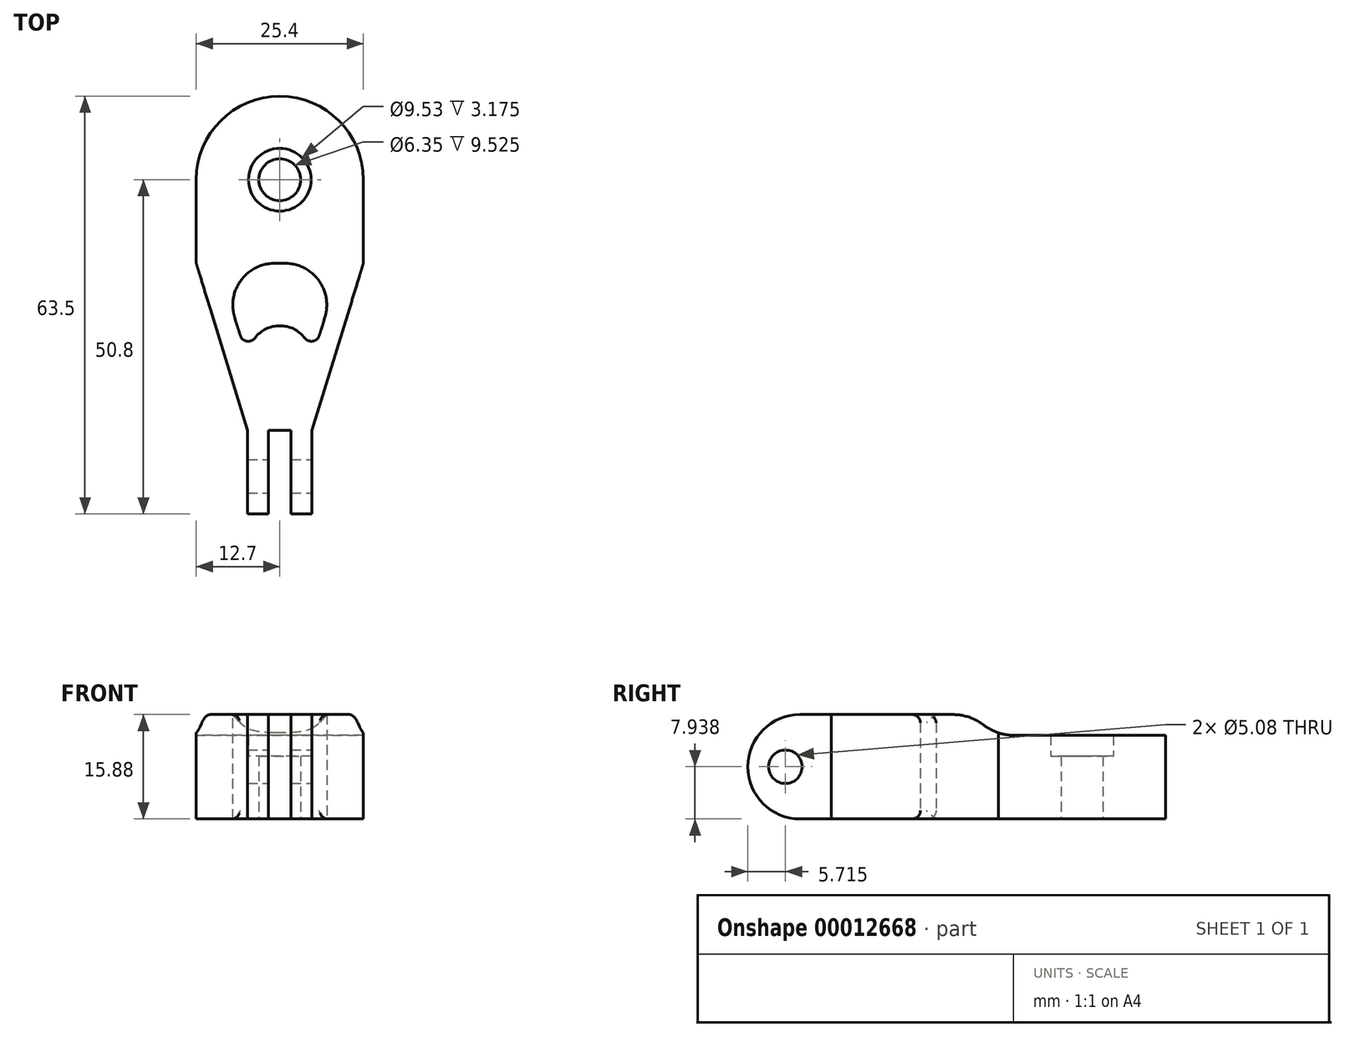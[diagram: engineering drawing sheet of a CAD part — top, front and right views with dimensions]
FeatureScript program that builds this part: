
annotation { "Feature Type Name" : "Feature", "Feature Type Description" : "" }
export const myFeature = defineFeature(function(context is Context, id is Id, definition is map)
    precondition{}
    {
        {
            var Q0;
            Q0=qCreatedBy(makeId("Top.planeOp"),FACE);
            var sketch = newSketch(context, id + "F0", { "sketchPlane" : qUnion([Q0])});
            skCircle(sketch, "E0", {"center": v(0, 0) * mm, "radius": 4.76 * mm});
            skCircle(sketch, "E1", {"center": v(0, 0) * mm, "radius": 12.7 * mm});
            skLineSegment(sketch, "E2.bottom", {"start": v(-12.7, 0) * mm, "end": v(12.7, 0) * mm});
            skLineSegment(sketch, "E2.top", {"start": v(-12.7, -50.8) * mm, "end": v(12.7, -50.8) * mm});
            skLineSegment(sketch, "E2.left", {"start": v(-12.7, 0) * mm, "end": v(-12.7, -50.8) * mm});
            skLineSegment(sketch, "E2.right", {"start": v(12.7, 0) * mm, "end": v(12.7, -50.8) * mm});
            skSolve(sketch);
        }
        {
            var Q0;
            {var subQ0=sQuery(id+"F0.wireOp",EDGE,"E2.bottom");var subQ1=sQuery(id+"F0.wireOp",EDGE,"E0");var subQ5=makeQuery(id+"F0.imprint","INTERSECT",VERTEX,{"disambiguationData":[OD(0.0)],"derivedFrom":[subQ1,subQ0]});Q0=makeQuery(id+"F0.imprint","IMPRINT",FACE,{"disambiguationData":[TD([[makeQuery(id+"F0.imprint","IMPRINT",EDGE,{"disambiguationData":[TD([[subQ5,1.0]])],"derivedFrom":subQ1}),-1.0]])]});}
            var Q1;
            {var subQ0=sQuery(id+"F0.wireOp",EDGE,"E2.bottom");var subQ1=sQuery(id+"F0.wireOp",EDGE,"E0");var subQ5=makeQuery(id+"F0.imprint","INTERSECT",VERTEX,{"disambiguationData":[OD(0.0)],"derivedFrom":[subQ1,subQ0]});Q1=makeQuery(id+"F0.imprint","IMPRINT",FACE,{"disambiguationData":[TD([[makeQuery(id+"F0.imprint","IMPRINT",EDGE,{"disambiguationData":[TD([[subQ5,-1.0]])],"derivedFrom":subQ1}),-1.0]])]});}
            var Q2;
            Q2=makeQuery(id+"F0.imprint","IMPRINT",FACE,{"disambiguationData":[TD([[makeQuery(id+"F0.imprint","IMPRINT",EDGE,{"derivedFrom":sQuery(id+"F0.wireOp",EDGE,"E2.top")}),1.0]])]});
            extrude(context, id + "F1", {"entities" : qUnion([Q0, Q1, Q2]), "depth" : 15.88 * mm});
        }
        {
            var Q0;
            Q0=qCreatedBy(makeId("Right.planeOp"),FACE);
            var sketch = newSketch(context, id + "F2", { "sketchPlane" : qUnion([Q0])});
            skLineSegment(sketch, "E3", {"start": v(12.7, 12.7) * mm, "end": v(-12.7, 12.7) * mm});
            skLineSegment(sketch, "E4", {"start": v(-12.7, 12.7) * mm, "end": v(-40.44, 32.12) * mm});
            skLineSegment(sketch, "E5", {"start": v(-40.44, 32.12) * mm, "end": v(12.7, 32.12) * mm});
            skLineSegment(sketch, "E6", {"start": v(12.7, 32.12) * mm, "end": v(12.7, 12.7) * mm});
            skSolve(sketch);
        }
        {
            var Q0;
            Q0=makeQuery(id+"F2.imprint","IMPRINT",FACE,{"disambiguationData":[TD([[makeQuery(id+"F2.imprint","IMPRINT",EDGE,{"derivedFrom":sQuery(id+"F2.wireOp",EDGE,"E3")}),-1.0]])]});
            extrude(context, id + "F3", {"entities" : qUnion([Q0]), "operationType" : NewBodyOperationType.REMOVE, "endBound" : BoundingType.SYMMETRIC, "oppositeDirection" : true, "depth" : 25.4 * mm});
        }
        {
            var Q0;
            Q0=makeQuery(id+"F1.opExtrude","CAP_FACE",FACE,{"disambiguationData":[OSD([sQuery(id+"F0.wireOp",EDGE,"E0"),sQuery(id+"F0.wireOp",EDGE,"E1"),sQuery(id+"F0.wireOp",EDGE,"E2.top"),sQuery(id+"F0.wireOp",EDGE,"E2.left"),sQuery(id+"F0.wireOp",EDGE,"E2.right")])],"isStart":false});
            var sketch = newSketch(context, id + "F4", { "sketchPlane" : qUnion([Q0])});
            skLineSegment(sketch, "E7.bottom", {"start": v(-4.9, -38.1) * mm, "end": v(-1.73, -38.1) * mm});
            skLineSegment(sketch, "E7.top", {"start": v(-4.9, -50.8) * mm, "end": v(-1.73, -50.8) * mm});
            skLineSegment(sketch, "E7.left", {"start": v(-4.9, -38.1) * mm, "end": v(-4.9, -50.8) * mm});
            skLineSegment(sketch, "E7.right", {"start": v(-1.73, -38.1) * mm, "end": v(-1.73, -50.8) * mm});
            skLineSegment(sketch, "E8.bottom", {"start": v(1.73, -38.1) * mm, "end": v(4.9, -38.1) * mm});
            skLineSegment(sketch, "E8.top", {"start": v(1.73, -50.8) * mm, "end": v(4.9, -50.8) * mm});
            skLineSegment(sketch, "E8.left", {"start": v(1.73, -38.1) * mm, "end": v(1.73, -50.8) * mm});
            skLineSegment(sketch, "E8.right", {"start": v(4.9, -38.1) * mm, "end": v(4.9, -50.8) * mm});
            skLineSegment(sketch, "E9.0.0", {"start": v(12.7, -50.8) * mm, "end": v(12.7, -17.23) * mm});
            skLineSegment(sketch, "E9.0.1", {"start": v(12.7, -17.23) * mm, "end": v(-12.7, -17.23) * mm});
            skLineSegment(sketch, "E9.0.2", {"start": v(-12.7, -17.23) * mm, "end": v(-12.7, -50.8) * mm});
            skLineSegment(sketch, "E9.0.3", {"start": v(-12.7, -50.8) * mm, "end": v(12.7, -50.8) * mm});
            skLineSegment(sketch, "E10", {"start": v(-1.73, -38.1) * mm, "end": v(1.73, -38.1) * mm});
            skLineSegment(sketch, "E11", {"start": v(4.9, -38.1) * mm, "end": v(12.7, -38.1) * mm});
            skLineSegment(sketch, "E12", {"start": v(-4.9, -38.1) * mm, "end": v(-12.7, -38.1) * mm});
            skSolve(sketch);
        }
        {
            var Q0;
            {var subQ2=sQuery(id+"F4.wireOp",EDGE,"E7.left");Q0=makeQuery(id+"F4.imprint","IMPRINT",FACE,{"disambiguationData":[TD([[makeQuery(id+"F4.imprint","IMPRINT",EDGE,{"derivedFrom":subQ2}),-1.0]])]});}
            var Q1;
            {var subQ2=sQuery(id+"F4.wireOp",EDGE,"E7.right");Q1=makeQuery(id+"F4.imprint","IMPRINT",FACE,{"disambiguationData":[TD([[makeQuery(id+"F4.imprint","IMPRINT",EDGE,{"derivedFrom":subQ2}),1.0]])]});}
            var Q2;
            {var subQ2=sQuery(id+"F4.wireOp",EDGE,"E8.right");Q2=makeQuery(id+"F4.imprint","IMPRINT",FACE,{"disambiguationData":[TD([[makeQuery(id+"F4.imprint","IMPRINT",EDGE,{"derivedFrom":subQ2}),1.0]])]});}
            extrude(context, id + "F5", {"entities" : qUnion([Q0, Q1, Q2]), "operationType" : NewBodyOperationType.REMOVE, "oppositeDirection" : true, "depth" : 25.4 * mm});
        }
        {
            var Q0;
            Q0=makeQuery(id+"F5.boolean.opBoolean","COPY",FACE,{"derivedFrom":makeQuery(id+"F5.opExtrude","SWEPT_FACE",FACE,{"disambiguationData":[OSD([sQuery(id+"F4.wireOp",EDGE,"E8.right")])]})});
            var sketch = newSketch(context, id + "F6", { "sketchPlane" : qUnion([Q0])});
            skCircle(sketch, "E13", {"center": v(-45.09, 7.94) * mm, "radius": 2.54 * mm});
            skSolve(sketch);
        }
        {
            var Q0;
            Q0 = qSketchRegion(id + "F6", true);
            extrude(context, id + "F7", {"entities" : qUnion([Q0]), "operationType" : NewBodyOperationType.REMOVE, "oppositeDirection" : true, "depth" : 25.4 * mm});
        }
        {
            var Q0;
            {var subQ0=sQuery(id+"F0.wireOp",EDGE,"E2.top");Q0=makeQuery(id+"F5.boolean.opBoolean","SPLIT",EDGE,{"disambiguationData":[TD([makeQuery(id+"F5.opExtrude","SWEPT_FACE",FACE,{"disambiguationData":[OSD([sQuery(id+"F4.wireOp",EDGE,"E8.left")])]})])],"derivedFrom":makeQuery(id+"F1.opExtrude","CAP_EDGE",EDGE,{"disambiguationData":[OSD([subQ0])],"isStart":false})});}
            var Q1;
            {var subQ0=sQuery(id+"F0.wireOp",EDGE,"E2.top");Q1=makeQuery(id+"F5.boolean.opBoolean","SPLIT",EDGE,{"disambiguationData":[TD([makeQuery(id+"F5.opExtrude","SWEPT_FACE",FACE,{"disambiguationData":[OSD([sQuery(id+"F4.wireOp",EDGE,"E7.left")])]})])],"derivedFrom":makeQuery(id+"F1.opExtrude","CAP_EDGE",EDGE,{"disambiguationData":[OSD([subQ0])],"isStart":false})});}
            var Q2;
            {var subQ0=sQuery(id+"F0.wireOp",EDGE,"E2.top");Q2=makeQuery(id+"F5.boolean.opBoolean","SPLIT",EDGE,{"disambiguationData":[TD([makeQuery(id+"F5.opExtrude","SWEPT_FACE",FACE,{"disambiguationData":[OSD([sQuery(id+"F4.wireOp",EDGE,"E7.left")])]})])],"derivedFrom":makeQuery(id+"F1.opExtrude","CAP_EDGE",EDGE,{"disambiguationData":[OSD([subQ0])],"isStart":true})});}
            var Q3;
            {var subQ0=sQuery(id+"F0.wireOp",EDGE,"E2.top");Q3=makeQuery(id+"F5.boolean.opBoolean","SPLIT",EDGE,{"disambiguationData":[TD([makeQuery(id+"F5.opExtrude","SWEPT_FACE",FACE,{"disambiguationData":[OSD([sQuery(id+"F4.wireOp",EDGE,"E8.left")])]})])],"derivedFrom":makeQuery(id+"F1.opExtrude","CAP_EDGE",EDGE,{"disambiguationData":[OSD([subQ0])],"isStart":true})});}
            fillet(context, id + "F8", {"entities" : qUnion([Q0, Q1, Q2, Q3]), "radius" : 7.94 * mm, "tangentPropagation" : true, "allowEdgeOverflow" : false});
        }
        {
            var Q0;
            Q0=qCreatedBy(makeId("Top.planeOp"),FACE);
            var sketch = newSketch(context, id + "F9", { "sketchPlane" : qUnion([Q0])});
            skLineSegment(sketch, "E14.0.0", {"start": v(-1.73, -38.1) * mm, "end": v(-1.73, -42.86) * mm});
            skLineSegment(sketch, "E14.0.1", {"start": v(-1.73, -42.86) * mm, "end": v(-4.9, -42.86) * mm});
            skLineSegment(sketch, "E14.0.2", {"start": v(-4.9, -42.86) * mm, "end": v(-4.9, -38.1) * mm});
            skLineSegment(sketch, "E14.0.3", {"start": v(-4.9, -38.1) * mm, "end": v(-12.7, -38.1) * mm});
            skLineSegment(sketch, "E14.0.4", {"start": v(-12.7, -38.1) * mm, "end": v(-12.7, 0) * mm});
            skArc(sketch, "E14.0.5", {"start": v(-12.7, 0) * mm, "mid": v(0, 12.7) * mm, "end": v(12.7, 0) * mm});
            skLineSegment(sketch, "E14.0.6", {"start": v(12.7, 0) * mm, "end": v(12.7, -38.1) * mm});
            skLineSegment(sketch, "E14.0.7", {"start": v(12.7, -38.1) * mm, "end": v(4.9, -38.1) * mm});
            skLineSegment(sketch, "E14.0.8", {"start": v(4.9, -38.1) * mm, "end": v(4.9, -42.86) * mm});
            skLineSegment(sketch, "E14.0.9", {"start": v(4.9, -42.86) * mm, "end": v(1.73, -42.86) * mm});
            skLineSegment(sketch, "E14.0.10", {"start": v(1.73, -42.86) * mm, "end": v(1.73, -38.1) * mm});
            skLineSegment(sketch, "E14.0.11", {"start": v(1.73, -38.1) * mm, "end": v(-1.73, -38.1) * mm});
            skLineSegment(sketch, "E15", {"start": v(4.9, -38.1) * mm, "end": v(12.7, -12.7) * mm});
            skLineSegment(sketch, "E16", {"start": v(-4.9, -38.1) * mm, "end": v(-12.7, -12.7) * mm});
            skSolve(sketch);
        }
        {
            var Q0;
            {var subQ2=sQuery(id+"F9.wireOp",EDGE,"E14.0.3");Q0=makeQuery(id+"F9.imprint","IMPRINT",FACE,{"disambiguationData":[TD([[makeQuery(id+"F9.imprint","IMPRINT",EDGE,{"derivedFrom":subQ2}),-1.0]])]});}
            var Q1;
            {var subQ1=sQuery(id+"F9.wireOp",EDGE,"E14.0.7");Q1=makeQuery(id+"F9.imprint","IMPRINT",FACE,{"disambiguationData":[TD([[makeQuery(id+"F9.imprint","IMPRINT",EDGE,{"derivedFrom":subQ1}),-1.0]])]});}
            extrude(context, id + "F10", {"entities" : qUnion([Q0, Q1]), "operationType" : NewBodyOperationType.REMOVE, "depth" : 25.4 * mm});
        }
        {
            var Q0;
            Q0=makeQuery(id+"F1.opExtrude","CAP_FACE",FACE,{"disambiguationData":[OSD([sQuery(id+"F0.wireOp",EDGE,"E0"),sQuery(id+"F0.wireOp",EDGE,"E1"),sQuery(id+"F0.wireOp",EDGE,"E2.top"),sQuery(id+"F0.wireOp",EDGE,"E2.left"),sQuery(id+"F0.wireOp",EDGE,"E2.right")])],"isStart":true});
            var sketch = newSketch(context, id + "F11", { "sketchPlane" : qUnion([Q0])});
            skLineSegment(sketch, "E17.0.0", {"start": v(-4.9, 38.1) * mm, "end": v(-12.7, 12.7) * mm});
            skLineSegment(sketch, "E17.0.1", {"start": v(-12.7, 12.7) * mm, "end": v(-12.7, 0) * mm});
            skArc(sketch, "E17.0.2", {"start": v(-12.7, 0) * mm, "mid": v(0, -12.7) * mm, "end": v(12.7, 0) * mm});
            skLineSegment(sketch, "E17.0.3", {"start": v(12.7, 0) * mm, "end": v(12.7, 12.7) * mm});
            skLineSegment(sketch, "E17.0.4", {"start": v(12.7, 12.7) * mm, "end": v(4.9, 38.1) * mm});
            skLineSegment(sketch, "E17.0.5", {"start": v(4.9, 38.1) * mm, "end": v(4.9, 42.86) * mm});
            skLineSegment(sketch, "E17.0.6", {"start": v(4.9, 42.86) * mm, "end": v(1.73, 42.86) * mm});
            skLineSegment(sketch, "E17.0.7", {"start": v(1.73, 42.86) * mm, "end": v(1.73, 38.1) * mm});
            skLineSegment(sketch, "E17.0.8", {"start": v(1.73, 38.1) * mm, "end": v(-1.73, 38.1) * mm});
            skLineSegment(sketch, "E17.0.9", {"start": v(-1.73, 38.1) * mm, "end": v(-1.73, 42.86) * mm});
            skLineSegment(sketch, "E17.0.10", {"start": v(-1.73, 42.86) * mm, "end": v(-4.9, 42.86) * mm});
            skLineSegment(sketch, "E17.0.11", {"start": v(-4.9, 42.86) * mm, "end": v(-4.9, 38.1) * mm});
            skLineSegment(sketch, "E18", {"start": v(0, 31.75) * mm, "end": v(0, 12.7) * mm});
            skLineSegment(sketch, "E19", {"start": v(12.7, 12.7) * mm, "end": v(0, 12.7) * mm});
            skCircle(sketch, "E20", {"center": v(0, 26.97) * mm, "radius": 4.78 * mm});
            skLineSegment(sketch, "E21", {"start": v(9.38, 12.7) * mm, "end": v(4.57, 28.38) * mm});
            skLineSegment(sketch, "E22", {"start": v(0, 12.7) * mm, "end": v(-12.7, 12.7) * mm});
            skLineSegment(sketch, "E23", {"start": v(-9.38, 12.7) * mm, "end": v(-4.57, 28.38) * mm});
            skSolve(sketch);
        }
        {
            var Q0;
            {var subQ0=sQuery(id+"F11.wireOp",EDGE,"E20");var subQ1=sQuery(id+"F11.wireOp",EDGE,"E18");var subQ4=makeQuery(id+"F11.imprint","INTERSECT",VERTEX,{"disambiguationData":[OD(0.0)],"derivedFrom":[subQ1,subQ0]});Q0=makeQuery(id+"F11.imprint","IMPRINT",FACE,{"disambiguationData":[TD([[makeQuery(id+"F11.imprint","IMPRINT",EDGE,{"disambiguationData":[TD([[subQ4,-1.0]])],"derivedFrom":subQ1}),-1.0]])]});}
            var Q1;
            {var subQ0=sQuery(id+"F11.wireOp",EDGE,"E20");var subQ1=sQuery(id+"F11.wireOp",EDGE,"E18");var subQ4=makeQuery(id+"F11.imprint","INTERSECT",VERTEX,{"disambiguationData":[OD(0.0)],"derivedFrom":[subQ1,subQ0]});Q1=makeQuery(id+"F11.imprint","IMPRINT",FACE,{"disambiguationData":[TD([[makeQuery(id+"F11.imprint","IMPRINT",EDGE,{"disambiguationData":[TD([[subQ4,-1.0]])],"derivedFrom":subQ1}),1.0]])]});}
            var Q2;
            {var subQ0=sQuery(id+"F11.wireOp",EDGE,"E21");Q2=makeQuery(id+"F11.imprint","IMPRINT",FACE,{"disambiguationData":[TD([[makeQuery(id+"F11.imprint","IMPRINT",EDGE,{"derivedFrom":subQ0}),1.0]])]});}
            var Q3;
            {var subQ0=sQuery(id+"F11.wireOp",EDGE,"E23");Q3=makeQuery(id+"F11.imprint","IMPRINT",FACE,{"disambiguationData":[TD([[makeQuery(id+"F11.imprint","IMPRINT",EDGE,{"derivedFrom":subQ0}),-1.0]])]});}
            extrude(context, id + "F12", {"entities" : qUnion([Q0, Q1, Q2, Q3]), "operationType" : NewBodyOperationType.REMOVE, "oppositeDirection" : true, "depth" : 25.4 * mm});
        }
        {
            var Q0;
            Q0=makeQuery(id+"F12.boolean.opBoolean","COPY",EDGE,{"derivedFrom":makeQuery(id+"F12.opExtrude","SWEPT_EDGE",EDGE,{"disambiguationData":[OSD([sQuery(id+"F11.wireOp",EDGE,"E22"),sQuery(id+"F11.wireOp",EDGE,"E23")])]})});
            var Q1;
            Q1=makeQuery(id+"F12.boolean.opBoolean","COPY",EDGE,{"derivedFrom":makeQuery(id+"F12.opExtrude","SWEPT_EDGE",EDGE,{"disambiguationData":[OSD([sQuery(id+"F11.wireOp",EDGE,"E19"),sQuery(id+"F11.wireOp",EDGE,"E21")])]})});
            fillet(context, id + "F13", {"entities" : qUnion([Q0, Q1]), "radius" : 6.35 * mm, "tangentPropagation" : true, "allowEdgeOverflow" : false});
        }
        {
            var Q0;
            {var subQ0=makeQuery(id+"F1.opExtrude","CAP_FACE",FACE,{"disambiguationData":[OSD([sQuery(id+"F0.wireOp",EDGE,"E0"),sQuery(id+"F0.wireOp",EDGE,"E1"),sQuery(id+"F0.wireOp",EDGE,"E2.top"),sQuery(id+"F0.wireOp",EDGE,"E2.left"),sQuery(id+"F0.wireOp",EDGE,"E2.right")])],"isStart":false});var subQ1=makeQuery(id+"F3.opExtrude","SWEPT_FACE",FACE,{"disambiguationData":[OSD([sQuery(id+"F2.wireOp",EDGE,"E4")])]});Q0=makeQuery(id+"F12.boolean.opBoolean","SPLIT",EDGE,{"disambiguationData":[TD([makeQuery(id+"F10.boolean.opBoolean","COPY",FACE,{"derivedFrom":makeQuery(id+"F10.opExtrude","SWEPT_FACE",FACE,{"disambiguationData":[OSD([sQuery(id+"F9.wireOp",EDGE,"E15")])]})})])],"derivedFrom":makeQuery(id+"F3.boolean.opBoolean","INTERSECT",EDGE,{"derivedFrom":[subQ0,subQ1]})});}
            var Q1;
            {var subQ0=makeQuery(id+"F1.opExtrude","CAP_FACE",FACE,{"disambiguationData":[OSD([sQuery(id+"F0.wireOp",EDGE,"E0"),sQuery(id+"F0.wireOp",EDGE,"E1"),sQuery(id+"F0.wireOp",EDGE,"E2.top"),sQuery(id+"F0.wireOp",EDGE,"E2.left"),sQuery(id+"F0.wireOp",EDGE,"E2.right")])],"isStart":false});var subQ1=makeQuery(id+"F3.opExtrude","SWEPT_FACE",FACE,{"disambiguationData":[OSD([sQuery(id+"F2.wireOp",EDGE,"E4")])]});Q1=makeQuery(id+"F12.boolean.opBoolean","SPLIT",EDGE,{"disambiguationData":[TD([makeQuery(id+"F10.boolean.opBoolean","COPY",FACE,{"derivedFrom":makeQuery(id+"F10.opExtrude","SWEPT_FACE",FACE,{"disambiguationData":[OSD([sQuery(id+"F9.wireOp",EDGE,"E16")])]})})])],"derivedFrom":makeQuery(id+"F3.boolean.opBoolean","INTERSECT",EDGE,{"derivedFrom":[subQ0,subQ1]})});}
            var Q2;
            {var subQ0=sQuery(id+"F2.wireOp",EDGE,"E3");var subQ1=sQuery(id+"F2.wireOp",EDGE,"E4");Q2=makeQuery(id+"F12.boolean.opBoolean","SPLIT",EDGE,{"disambiguationData":[TD([makeQuery(id+"F1.opExtrude","SWEPT_FACE",FACE,{"disambiguationData":[OSD([sQuery(id+"F0.wireOp",EDGE,"E2.left")])]}),makeQuery(id+"F3.boolean.opBoolean","COPY",FACE,{"derivedFrom":makeQuery(id+"F3.opExtrude","SWEPT_FACE",FACE,{"disambiguationData":[OSD([subQ0])]})}),makeQuery(id+"F3.boolean.opBoolean","COPY",FACE,{"derivedFrom":makeQuery(id+"F3.opExtrude","SWEPT_FACE",FACE,{"disambiguationData":[OSD([subQ1])]})}),makeQuery(id+"F10.boolean.opBoolean","COPY",FACE,{"derivedFrom":makeQuery(id+"F10.opExtrude","SWEPT_FACE",FACE,{"disambiguationData":[OSD([sQuery(id+"F9.wireOp",EDGE,"E16")])]})}),makeQuery(id+"F12.opExtrude","SWEPT_FACE",FACE,{"disambiguationData":[OSD([sQuery(id+"F11.wireOp",EDGE,"E19"),sQuery(id+"F11.wireOp",EDGE,"E22")])]}),makeQuery(id+"F12.opExtrude","SWEPT_FACE",FACE,{"disambiguationData":[OSD([sQuery(id+"F11.wireOp",EDGE,"E23")])]})])],"derivedFrom":makeQuery(id+"F3.boolean.opBoolean","COPY",EDGE,{"derivedFrom":makeQuery(id+"F3.opExtrude","SWEPT_EDGE",EDGE,{"disambiguationData":[OSD([subQ0,subQ1])]})})});}
            fillet(context, id + "F14", {"entities" : qUnion([Q0, Q1, Q2]), "radius" : 7.62 * mm, "tangentPropagation" : true, "allowEdgeOverflow" : false});
        }
        {
            var Q0;
            Q0=makeQuery(id+"F12.boolean.opBoolean","COPY",FACE,{"derivedFrom":makeQuery(id+"F12.opExtrude","SWEPT_FACE",FACE,{"disambiguationData":[OSD([sQuery(id+"F11.wireOp",EDGE,"E20")])]})});
            fillet(context, id + "F15", {"entities" : qUnion([Q0]), "radius" : 1.27 * mm, "tangentPropagation" : true, "allowEdgeOverflow" : false});
        }
        {
            var Q0;
            Q0=makeQuery(id+"F1.opExtrude","CAP_FACE",FACE,{"disambiguationData":[OSD([sQuery(id+"F0.wireOp",EDGE,"E0"),sQuery(id+"F0.wireOp",EDGE,"E1"),sQuery(id+"F0.wireOp",EDGE,"E2.top"),sQuery(id+"F0.wireOp",EDGE,"E2.left"),sQuery(id+"F0.wireOp",EDGE,"E2.right")])],"isStart":true});
            var sketch = newSketch(context, id + "F16", { "sketchPlane" : qUnion([Q0])});
            skCircle(sketch, "E24", {"center": v(0, 0) * mm, "radius": 3.18 * mm});
            skCircle(sketch, "E25.0", {"center": v(0, 0) * mm, "radius": 4.76 * mm});
            skSolve(sketch);
        }
        {
            var Q0;
            Q0=makeQuery(id+"F16.imprint","IMPRINT",FACE,{"disambiguationData":[TD([[makeQuery(id+"F16.imprint","IMPRINT",EDGE,{"derivedFrom":sQuery(id+"F16.wireOp",EDGE,"E24")}),-1.0]])]});
            extrude(context, id + "F17", {"entities" : qUnion([Q0]), "operationType" : NewBodyOperationType.ADD, "oppositeDirection" : true, "depth" : 9.52 * mm});
        }
    });
